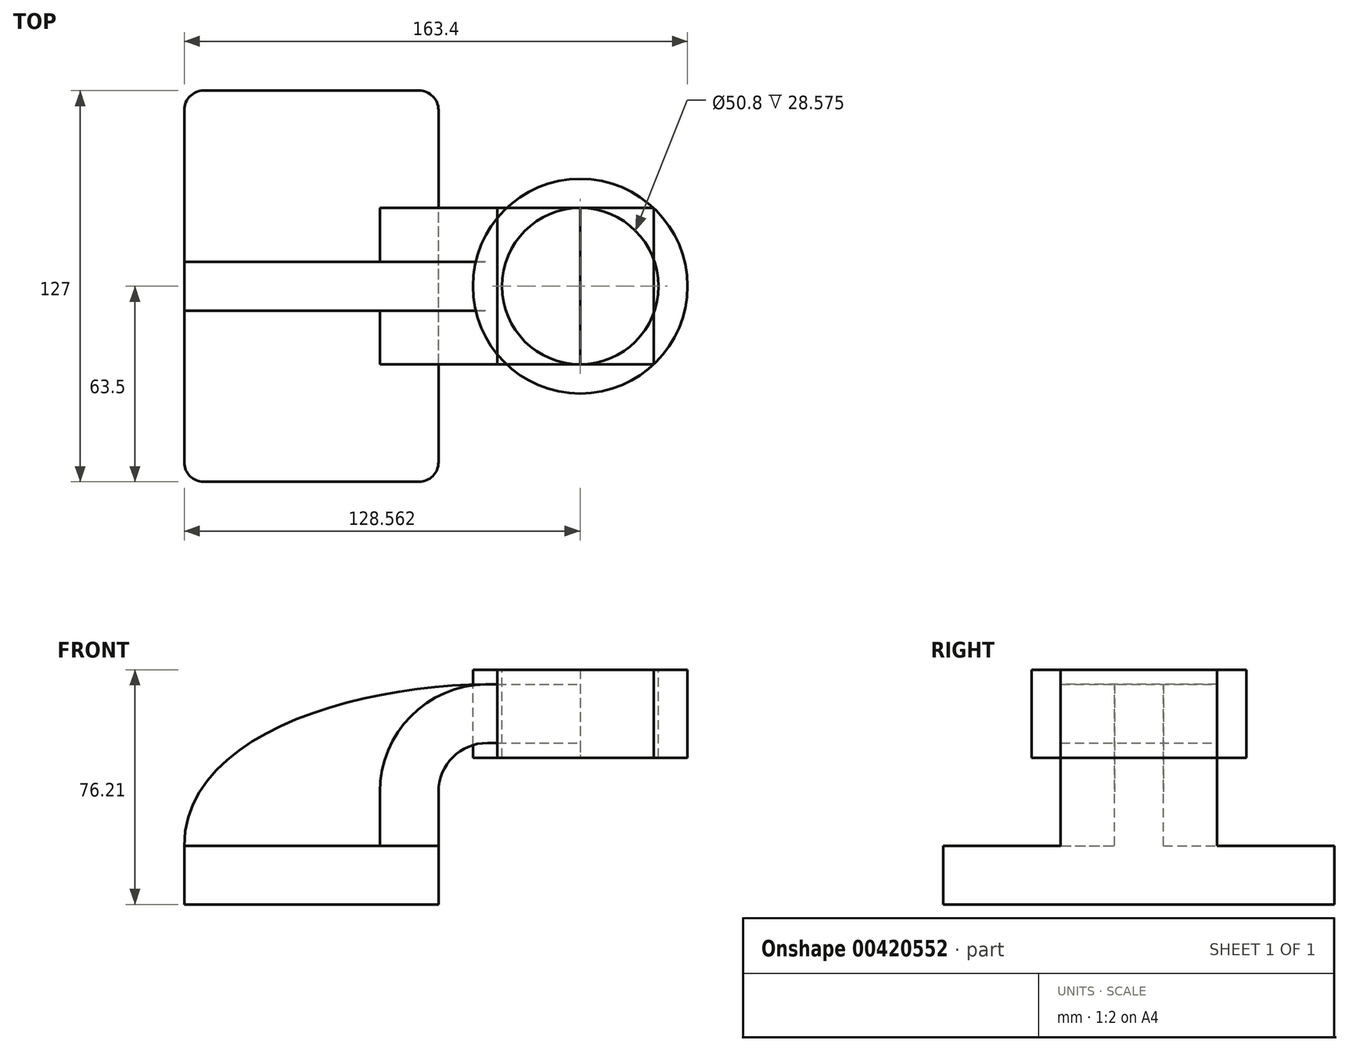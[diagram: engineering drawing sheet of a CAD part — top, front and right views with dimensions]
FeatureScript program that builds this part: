
annotation { "Feature Type Name" : "Feature", "Feature Type Description" : "" }
export const myFeature = defineFeature(function(context is Context, id is Id, definition is map)
    precondition{}
    {
        {
            var Q0;
            Q0=qCreatedBy(makeId("Front.planeOp"),FACE);
            var sketch = newSketch(context, id + "F0", { "sketchPlane" : qUnion([Q0])});
            skLineSegment(sketch, "E0.bottom", {"start": v(41.27, 9.53) * mm, "end": v(-41.28, 9.53) * mm});
            skLineSegment(sketch, "E0.top", {"start": v(41.28, -9.52) * mm, "end": v(-41.27, -9.52) * mm});
            skLineSegment(sketch, "E0.left", {"start": v(41.28, 9.53) * mm, "end": v(41.28, -9.52) * mm});
            skLineSegment(sketch, "E0.right", {"start": v(-41.28, 9.53) * mm, "end": v(-41.27, -9.52) * mm});
            skPoint(sketch, "E0.middle", {"position": v(0, 0) * mm});
            skLineSegment(sketch, "E1.bottom", {"start": v(60.33, 66.68) * mm, "end": v(111.13, 66.68) * mm});
            skLineSegment(sketch, "E1.top", {"start": v(60.33, 38.1) * mm, "end": v(111.13, 38.1) * mm});
            skLineSegment(sketch, "E1.left", {"start": v(60.33, 66.68) * mm, "end": v(60.33, 38.1) * mm});
            skLineSegment(sketch, "E1.right", {"start": v(111.13, 66.68) * mm, "end": v(111.13, 38.1) * mm});
            skPoint(sketch, "E1.middle", {"position": v(85.73, 52.39) * mm});
            skLineSegment(sketch, "E2", {"start": v(41.27, 9.53) * mm, "end": v(41.27, 27) * mm});
            skArc(sketch, "E3", {"start": v(41.27, 27) * mm, "mid": v(45.92, 38.23) * mm, "end": v(57.15, 42.88) * mm});
            skLineSegment(sketch, "E4", {"start": v(57.15, 42.88) * mm, "end": v(87.28, 42.88) * mm});
            skLineSegment(sketch, "E5.0", {"start": v(57.15, 61.93) * mm, "end": v(87.28, 61.93) * mm});
            skArc(sketch, "E5.1", {"start": v(22.23, 27) * mm, "mid": v(32.45, 51.7) * mm, "end": v(57.15, 61.93) * mm});
            skLineSegment(sketch, "E5.2", {"start": v(22.22, 9.53) * mm, "end": v(22.22, 27) * mm});
            skLineSegment(sketch, "E6", {"start": v(87.28, 66.68) * mm, "end": v(87.28, 38.1) * mm});
            skPoint(sketch, "E6.startSnap0", {"position": v(85.73, 66.68) * mm});
            skFitSpline(sketch, "E7", {"points": [v(-41.28, 9.52) * mm, v(57.15, 61.93) * mm], "startDerivative": vector(1, 111.8) * mm, "endDerivative": vector(122, 0.73) * mm});
            skSolve(sketch);
        }
        {
            var Q0;
            Q0=makeQuery(id+"F0.imprint","IMPRINT",FACE,{"disambiguationData":[TD([[makeQuery(id+"F0.imprint","IMPRINT",EDGE,{"derivedFrom":sQuery(id+"F0.wireOp",EDGE,"E0.top")}),-1.0]])]});
            extrude(context, id + "F1", {"entities" : qUnion([Q0]), "endBound" : BoundingType.SYMMETRIC, "depth" : 127 * mm});
        }
        {
            var Q0;
            {var subQ3=sQuery(id+"F0.wireOp",EDGE,"E5.2");Q0=makeQuery(id+"F0.imprint","IMPRINT",FACE,{"disambiguationData":[TD([[makeQuery(id+"F0.imprint","IMPRINT",EDGE,{"derivedFrom":subQ3}),1.0]])]});}
            extrude(context, id + "F2", {"entities" : qUnion([Q0]), "operationType" : NewBodyOperationType.ADD, "endBound" : BoundingType.SYMMETRIC, "depth" : 15.88 * mm});
        }
        {
            var Q0;
            {var subQ1=sQuery(id+"F0.wireOp",EDGE,"E2");Q0=makeQuery(id+"F0.imprint","IMPRINT",FACE,{"disambiguationData":[TD([[makeQuery(id+"F0.imprint","IMPRINT",EDGE,{"derivedFrom":subQ1}),1.0]])]});}
            extrude(context, id + "F3", {"entities" : qUnion([Q0]), "operationType" : NewBodyOperationType.ADD, "endBound" : BoundingType.SYMMETRIC, "depth" : 50.8 * mm});
        }
        {
            var Q0;
            {var subQ0=sQuery(id+"F0.wireOp",EDGE,"E1.left");var subQ1=sQuery(id+"F0.wireOp",EDGE,"E1.bottom");var subQ2=makeQuery(id+"F0.imprint","INTERSECT",VERTEX,{"derivedFrom":[subQ1,subQ0]});Q0=makeQuery(id+"F0.imprint","IMPRINT",FACE,{"disambiguationData":[TD([[makeQuery(id+"F0.imprint","IMPRINT",EDGE,{"disambiguationData":[TD([[subQ2,-1.0]])],"derivedFrom":subQ1}),-1.0]])]});}
            extrude(context, id + "F4", {"entities" : qUnion([Q0]), "endBound" : BoundingType.SYMMETRIC, "depth" : 50.8 * mm});
        }
        {
            var Q0;
            {var subQ0=sQuery(id+"F0.wireOp",EDGE,"E1.left");var subQ1=sQuery(id+"F0.wireOp",EDGE,"E1.top");var subQ2=makeQuery(id+"F0.imprint","INTERSECT",VERTEX,{"derivedFrom":[subQ1,subQ0]});Q0=makeQuery(id+"F0.imprint","IMPRINT",FACE,{"disambiguationData":[TD([[makeQuery(id+"F0.imprint","IMPRINT",EDGE,{"disambiguationData":[TD([[subQ2,-1.0]])],"derivedFrom":subQ1}),1.0]])]});}
            extrude(context, id + "F5", {"entities" : qUnion([Q0]), "endBound" : BoundingType.SYMMETRIC, "depth" : 50.8 * mm});
        }
        {
            var Q0;
            {var subQ0=sQuery(id+"F0.wireOp",EDGE,"E5.0");var subQ1=sQuery(id+"F0.wireOp",EDGE,"E1.left");var subQ2=makeQuery(id+"F0.imprint","INTERSECT",VERTEX,{"derivedFrom":[subQ1,subQ0]});Q0=makeQuery(id+"F0.imprint","IMPRINT",FACE,{"disambiguationData":[TD([[makeQuery(id+"F0.imprint","IMPRINT",EDGE,{"disambiguationData":[TD([[subQ2,-1.0]])],"derivedFrom":subQ1}),1.0]])]});}
            extrude(context, id + "F6", {"entities" : qUnion([Q0]), "endBound" : BoundingType.SYMMETRIC, "depth" : 50.8 * mm});
        }
        {
            var Q0;
            {var subQ4=sQuery(id+"F0.wireOp",EDGE,"E1.right");Q0=makeQuery(id+"F0.imprint","IMPRINT",FACE,{"disambiguationData":[TD([[makeQuery(id+"F0.imprint","IMPRINT",EDGE,{"derivedFrom":subQ4}),-1.0]])]});}
            extrude(context, id + "F7", {"entities" : qUnion([Q0]), "endBound" : BoundingType.SYMMETRIC, "depth" : 50.8 * mm});
        }
        {
            var Q0;
            Q0=makeQuery(id+"F7.opExtrude","CAP_FACE",FACE,{"disambiguationData":[OSD([sQuery(id+"F0.wireOp",EDGE,"E1.bottom"),sQuery(id+"F0.wireOp",EDGE,"E1.top"),sQuery(id+"F0.wireOp",EDGE,"E1.right"),sQuery(id+"F0.wireOp",EDGE,"E6")])],"isStart":true});
            var Q1;
            Q1=sQuery(id+"F0.wireOp",EDGE,"E6");
            revolve(context, id + "F8", {"entities" : qUnion([Q0]), "axis" : qUnion([Q1]), "revolveType" : RevolveType.FULL});
        }
        {
            var Q0;
            Q0=makeQuery(id+"F1.opExtrude","CAP_EDGE",EDGE,{"disambiguationData":[OSD([sQuery(id+"F0.wireOp",EDGE,"E0.left")])],"isStart":false});
            var Q1;
            Q1=makeQuery(id+"F1.opExtrude","CAP_EDGE",EDGE,{"disambiguationData":[OSD([sQuery(id+"F0.wireOp",EDGE,"E0.left")])],"isStart":true});
            var Q2;
            Q2=makeQuery(id+"F1.opExtrude","CAP_EDGE",EDGE,{"disambiguationData":[OSD([sQuery(id+"F0.wireOp",EDGE,"E0.right")])],"isStart":false});
            var Q3;
            Q3=makeQuery(id+"F1.opExtrude","CAP_EDGE",EDGE,{"disambiguationData":[OSD([sQuery(id+"F0.wireOp",EDGE,"E0.right")])],"isStart":true});
            fillet(context, id + "F9", {"entities" : qUnion([Q0, Q1, Q2, Q3]), "radius" : 6.35 * mm, "tangentPropagation" : true, "allowEdgeOverflow" : false});
        }
    });
